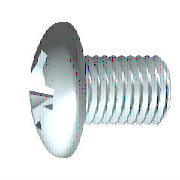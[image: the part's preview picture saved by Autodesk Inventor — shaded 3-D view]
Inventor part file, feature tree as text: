
AUTODESK INVENTOR PART (.ipt)
format: ipt  version: 2018 (Build 220112000, 112)  size: 330,240 bytes
history: native  units: mm (DEFAULTED — no unit token found)
features: other x2, extrude x2, plane x1
ambient origin geometry x7: Origin, YZ Plane, XZ Plane, X Axis, Y Axis, Z Axis, Center Point
bodies: Solid1 (feature_tree), Body (feature_tree)
feature tree (5):
  other  "IDS_WORKPLANE{1}"
  extrude  "Slot"  Depth=2.0mm
  other  "Cut"
  extrude  "Star Cut"  Depth=1.4mm
  plane  "Work Plane3"
